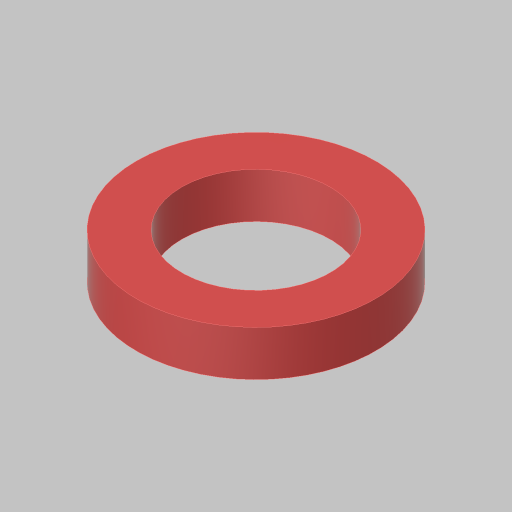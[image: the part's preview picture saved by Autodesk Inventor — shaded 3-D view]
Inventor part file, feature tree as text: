
AUTODESK INVENTOR PART (.ipt)
format: ipt  version: 2023.5 (Build 275446000, 446)  size: 96,256 bytes
history: native  units: in
note: dims shown in document units (in); Inventor stores cm internally (conversion verified against a paired STEP export)
features: extrude x1, sketch x1
ambient origin geometry x8: Origin, YZ Plane, XZ Plane, XY Plane, X Axis, Y Axis, Z Axis, Center Point
bodies: Solid1 (feature_tree)
feature tree (2):
  extrude  "Extrusion1"  Depth=0.125in
  sketch  "Sketch1"  dims[d0=0.41in d1=0.125in d2=0.125in d3=0.0in]
